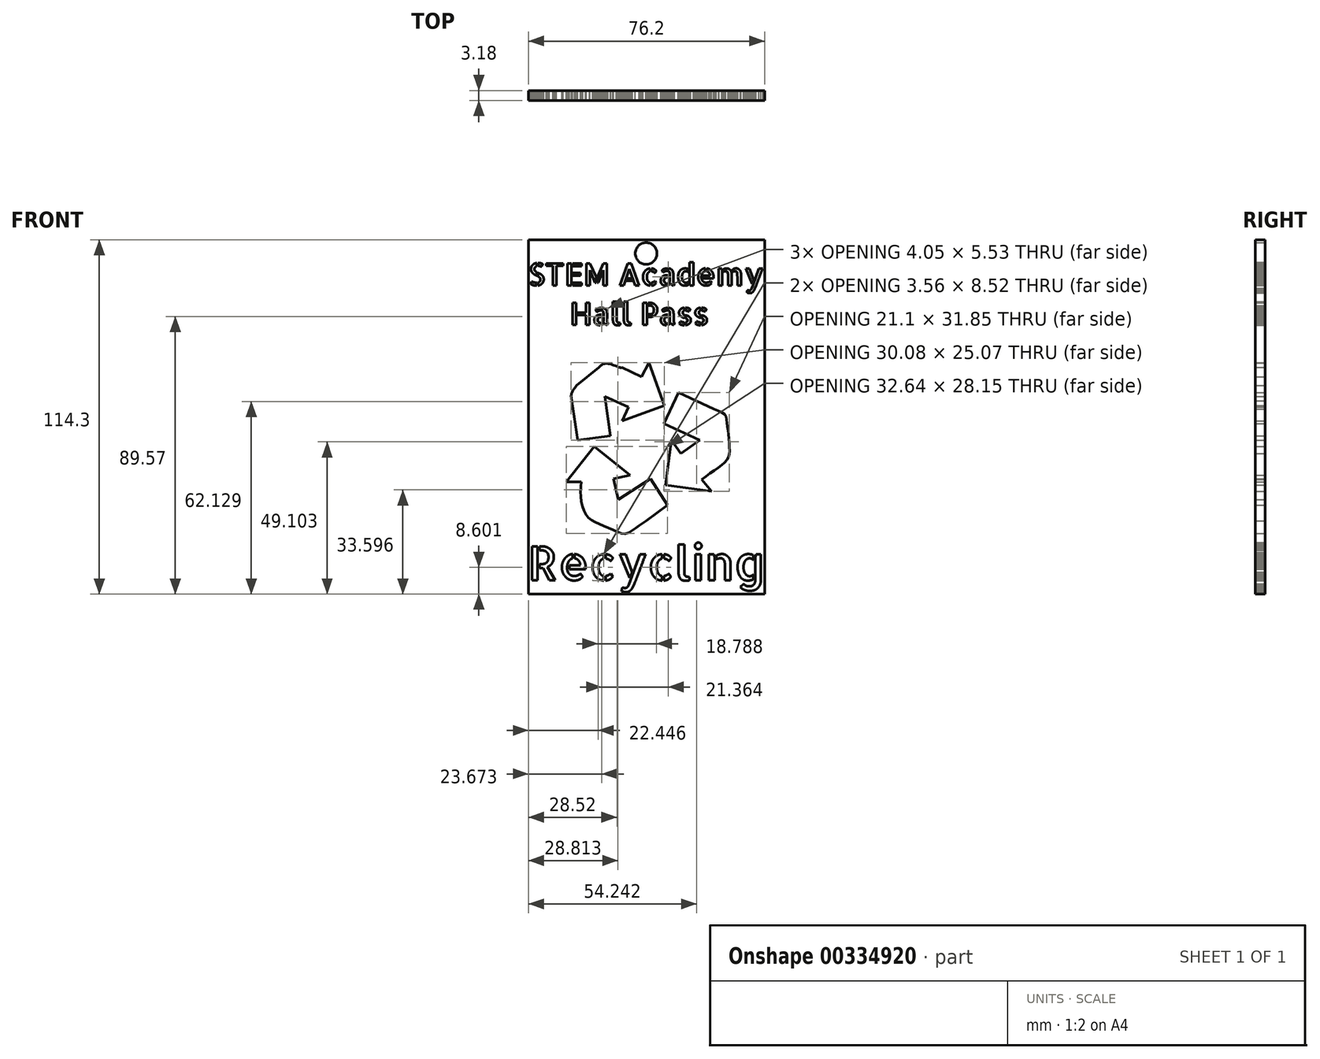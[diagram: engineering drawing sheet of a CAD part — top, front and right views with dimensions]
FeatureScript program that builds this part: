
annotation { "Feature Type Name" : "Feature", "Feature Type Description" : "" }
export const myFeature = defineFeature(function(context is Context, id is Id, definition is map)
    precondition{}
    {
        {
            var Q0;
            Q0=qCreatedBy(makeId("Front.planeOp"),FACE);
            var sketch = newSketch(context, id + "F0", { "sketchPlane" : qUnion([Q0])});
            skLineSegment(sketch, "E0.bottom", {"start": v(-37.96, 56.5) * mm, "end": v(38.24, 56.5) * mm});
            skLineSegment(sketch, "E0.top", {"start": v(-37.96, -57.8) * mm, "end": v(38.24, -57.8) * mm});
            skLineSegment(sketch, "E0.left", {"start": v(-37.96, 56.5) * mm, "end": v(-37.96, -57.8) * mm});
            skLineSegment(sketch, "E0.right", {"start": v(38.24, 56.5) * mm, "end": v(38.24, -57.8) * mm});
            skSolve(sketch);
        }
        {
            var Q0;
            Q0=qCreatedBy(makeId("Front.planeOp"),FACE);
            var sketch = newSketch(context, id + "F1", { "sketchPlane" : qUnion([Q0])});
            skSolve(sketch);
        }
        {
            var Q0;
            Q0 = qSketchRegion(id + "F1", true);
            var Q1;
            Q1=makeQuery(id+"F0.imprint","IMPRINT",FACE,{"disambiguationData":[TD([[makeQuery(id+"F0.imprint","IMPRINT",EDGE,{"derivedFrom":sQuery(id+"F0.wireOp",EDGE,"E0.bottom")}),-1.0]])]});
            extrude(context, id + "F2", {"entities" : qUnion([Q0, Q1]), "depth" : 3.17 * mm});
        }
        {
            var Q0;
            Q0=qCreatedBy(makeId("Front.planeOp"),FACE);
            var sketch = newSketch(context, id + "F3", { "sketchPlane" : qUnion([Q0])});
            skText(sketch, "E1", { "text": "STEM Academy\n     Hall Pass", "fontName": "AllertaStencil-Regular.ttf"});
            const initialGuessF3  = {"E1": [-0.038, 0.04176, 1, 0, 0.00717]};
            skSetInitialGuess(sketch, initialGuessF3);
            skSolve(sketch);
        }
        {
            var Q0;
            Q0 = qSketchRegion(id + "F3", true);
            var Q1;
            Q1 = qConstructionFilter(qBodyType(qCreatedBy(id + "F3" ,EDGE), BodyType.WIRE), ConstructionObject.NO);
            extrude(context, id + "F4", {"entities" : qUnion([Q0]), "operationType" : NewBodyOperationType.REMOVE, "surfaceEntities" : qUnion([Q1]), "depth" : 3.3 * mm});
        }
        {
            var Q0;
            Q0=qCreatedBy(makeId("Front.planeOp"),FACE);
            var sketch = newSketch(context, id + "F5", { "sketchPlane" : qUnion([Q0])});
            skLineSegment(sketch, "E2", {"start": v(-13.3, 5.94) * mm, "end": v(-5.75, 2.5) * mm});
            skLineSegment(sketch, "E3", {"start": v(-5.75, 2.5) * mm, "end": v(-7.78, -1.96) * mm});
            skLineSegment(sketch, "E4", {"start": v(-7.78, -1.96) * mm, "end": v(5.9, 2.99) * mm});
            skLineSegment(sketch, "E5", {"start": v(5.9, 2.99) * mm, "end": v(0.87, 16.86) * mm});
            skLineSegment(sketch, "E6", {"start": v(0.87, 16.86) * mm, "end": v(-1.49, 12.34) * mm});
            skLineSegment(sketch, "E7", {"start": v(-13.3, 5.94) * mm, "end": v(-11.49, -6.69) * mm});
            skLineSegment(sketch, "E8", {"start": v(-11.49, -6.69) * mm, "end": v(-22.12, -8.2) * mm});
            skLineSegment(sketch, "E9", {"start": v(-22.12, -8.2) * mm, "end": v(-23.95, 4.6) * mm});
            skFitSpline(sketch, "E10", {"points": [v(-23.95, 4.6) * mm, v(-23.95, 7.25) * mm, v(-22.48, 9.55) * mm, v(-22.64, 9.55) * mm], "startDerivative": vector(-1.44, 5.67) * mm, "endDerivative": vector(-2.1, -0.54) * mm});
            skLineSegment(sketch, "E11", {"start": v(-22.48, 9.55) * mm, "end": v(-15.26, 15.3) * mm});
            skFitSpline(sketch, "E12", {"points": [v(-15.26, 15.3) * mm, v(-12.97, 16.6) * mm, v(-8.37, 15.3) * mm, v(-7.88, 15.3) * mm], "startDerivative": vector(5.06, 5.4) * mm, "endDerivative": vector(2.18, 0.62) * mm});
            skLineSegment(sketch, "E13", {"start": v(-7.88, 15.3) * mm, "end": v(-1.49, 12.34) * mm});
            skLineSegment(sketch, "E14", {"start": v(8.2, -8.16) * mm, "end": v(6.22, -22.6) * mm});
            skLineSegment(sketch, "E15", {"start": v(6.22, -22.6) * mm, "end": v(21.09, -24.62) * mm});
            skLineSegment(sketch, "E16", {"start": v(21.09, -24.62) * mm, "end": v(17.87, -20.8) * mm});
            skLineSegment(sketch, "E17", {"start": v(8.2, -8.16) * mm, "end": v(11.14, -12.43) * mm});
            skLineSegment(sketch, "E18", {"start": v(11.14, -12.43) * mm, "end": v(17.3, -8.16) * mm});
            skLineSegment(sketch, "E19", {"start": v(17.3, -8.16) * mm, "end": v(5.73, -2.75) * mm});
            skLineSegment(sketch, "E20", {"start": v(5.73, -2.75) * mm, "end": v(10.4, 7.23) * mm});
            skLineSegment(sketch, "E21", {"start": v(10.4, 7.23) * mm, "end": v(21.85, 1.87) * mm});
            skFitSpline(sketch, "E22", {"points": [v(21.85, 1.87) * mm, v(25.41, 0) * mm, v(26.07, -2.42) * mm, v(26.56, -6.52) * mm, v(26.89, -11.28) * mm, v(26.4, -14.07) * mm, v(23.6, -16.7) * mm, v(17.87, -20.8) * mm], "startDerivative": vector(30.53, -11.1) * mm, "endDerivative": vector(-32.38, -22.88) * mm});
            skLineSegment(sketch, "E23", {"start": v(-16.74, -10.13) * mm, "end": v(-25.76, -21.61) * mm});
            skLineSegment(sketch, "E24", {"start": v(-25.76, -21.61) * mm, "end": v(-21, -21.61) * mm});
            skFitSpline(sketch, "E25", {"points": [v(-21, -21.61) * mm, v(-21, -27.35) * mm, v(-19.36, -32.27) * mm, v(-16.41, -34.57) * mm, v(-11.16, -36.86) * mm, v(-6.9, -38.34) * mm, v(-3.45, -36.54) * mm, v(0, -34.24) * mm], "startDerivative": vector(-2.24, -36.16) * mm, "endDerivative": vector(25.64, 16.3) * mm});
            skFitSpline(sketch, "E26", {"points": [v(0, -34.24) * mm, v(6.88, -29.16) * mm], "startDerivative": vector(6.88, 5.08) * mm, "endDerivative": vector(6.88, 5.08) * mm});
            skLineSegment(sketch, "E27", {"start": v(6.88, -29.16) * mm, "end": v(1.47, -20.63) * mm});
            skLineSegment(sketch, "E28", {"start": v(1.47, -20.63) * mm, "end": v(-9.06, -27.3) * mm});
            skLineSegment(sketch, "E29", {"start": v(-9.06, -27.3) * mm, "end": v(-10.5, -20.63) * mm});
            skLineSegment(sketch, "E30", {"start": v(-10.5, -20.63) * mm, "end": v(-5.13, -19.46) * mm});
            skLineSegment(sketch, "E31", {"start": v(-5.13, -19.46) * mm, "end": v(-16.74, -10.13) * mm});
            skSolve(sketch);
        }
        {
            var Q0;
            Q0 = qSketchRegion(id + "F5", true);
            extrude(context, id + "F6", {"entities" : qUnion([Q0]), "operationType" : NewBodyOperationType.REMOVE, "depth" : 25.4 * mm});
        }
        {
            var Q0;
            Q0=qCreatedBy(makeId("Front.planeOp"),FACE);
            var sketch = newSketch(context, id + "F7", { "sketchPlane" : qUnion([Q0])});
            skText(sketch, "E32", { "text": "Recycling ", "fontName": "AllertaStencil-Regular.ttf"});
            const initialGuessF7  = {"E32": [-0.03813, -0.0534, 1, 0, 0.01102]};
            skSetInitialGuess(sketch, initialGuessF7);
            skSolve(sketch);
        }
        {
            var Q0;
            Q0 = qSketchRegion(id + "F7", true);
            extrude(context, id + "F8", {"entities" : qUnion([Q0]), "operationType" : NewBodyOperationType.REMOVE, "depth" : 25.4 * mm});
        }
        {
            var Q0;
            Q0=qCreatedBy(makeId("Front.planeOp"),FACE);
            var sketch = newSketch(context, id + "F9", { "sketchPlane" : qUnion([Q0])});
            skCircle(sketch, "E33", {"center": v(0, 52.1) * mm, "radius": 3.5 * mm});
            skSolve(sketch);
        }
        {
            var Q0;
            Q0 = qSketchRegion(id + "F9", true);
            extrude(context, id + "F10", {"entities" : qUnion([Q0]), "operationType" : NewBodyOperationType.REMOVE, "depth" : 25.4 * mm});
        }
    });
